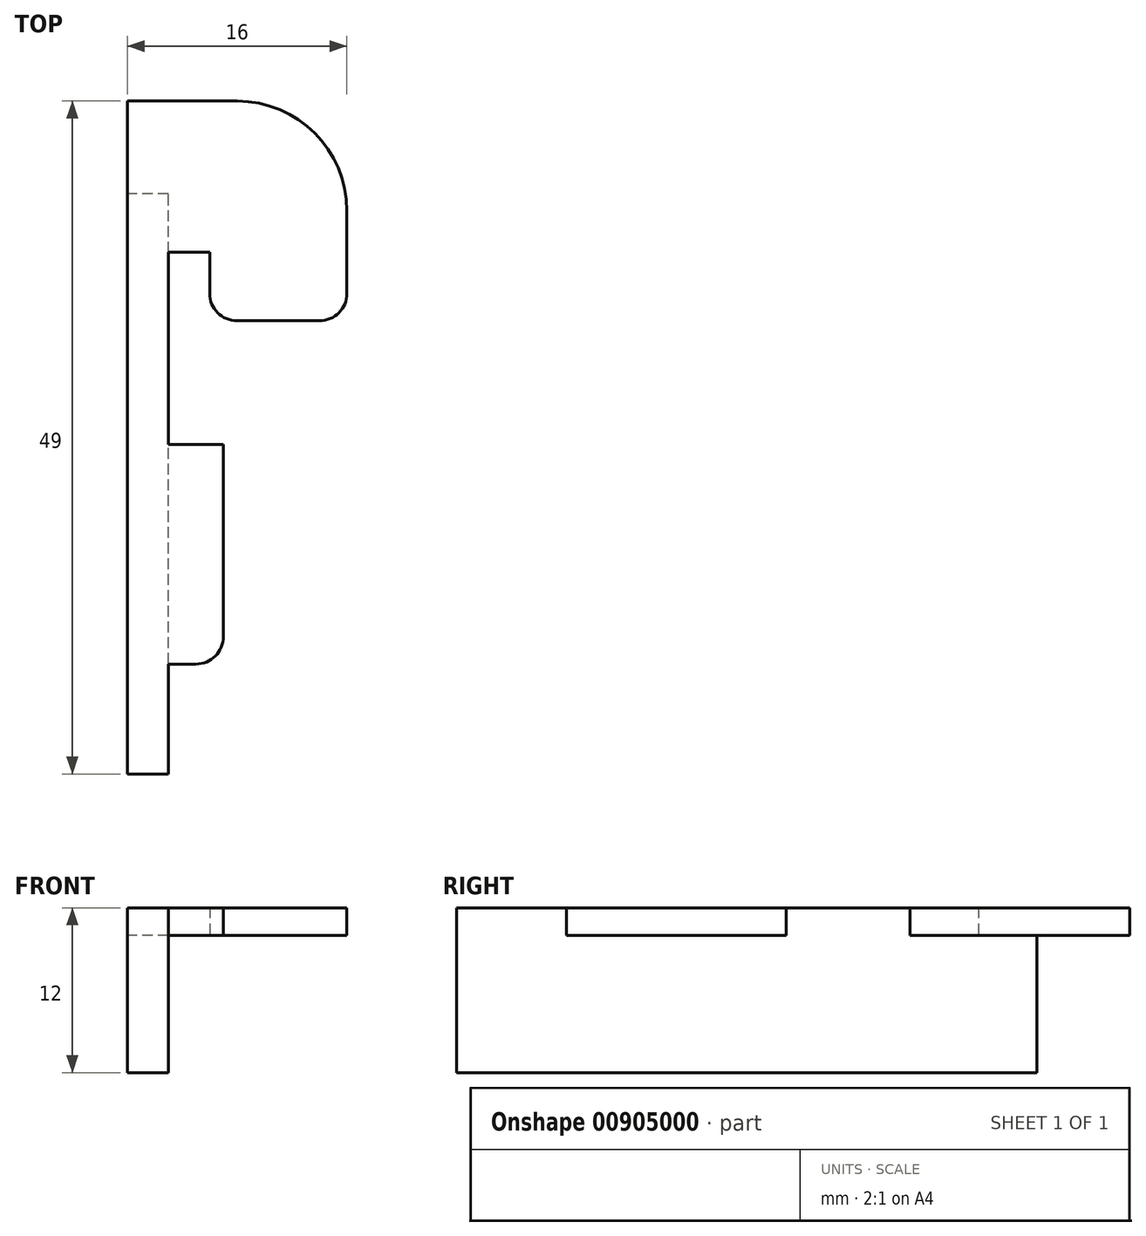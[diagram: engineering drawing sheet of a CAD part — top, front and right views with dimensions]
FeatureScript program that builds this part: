
annotation { "Feature Type Name" : "Feature", "Feature Type Description" : "" }
export const myFeature = defineFeature(function(context is Context, id is Id, definition is map)
    precondition{}
    {
        {
            var Q0;
            Q0=qCreatedBy(makeId("Top.planeOp"),FACE);
            var sketch = newSketch(context, id + "F0", { "sketchPlane" : qUnion([Q0])});
            skLineSegment(sketch, "E0", {"start": v(5, 25) * mm, "end": v(5, -24) * mm});
            skLineSegment(sketch, "E1", {"start": v(5, -24) * mm, "end": v(8, -24) * mm});
            skLineSegment(sketch, "E2", {"start": v(8, -24) * mm, "end": v(8, -16) * mm});
            skLineSegment(sketch, "E3", {"start": v(8, -16) * mm, "end": v(12, -16) * mm});
            skLineSegment(sketch, "E4", {"start": v(12, -16) * mm, "end": v(12, 0) * mm});
            skLineSegment(sketch, "E5", {"start": v(12, 0) * mm, "end": v(8, 0) * mm});
            skLineSegment(sketch, "E6", {"start": v(8, 0) * mm, "end": v(8, 14) * mm});
            skLineSegment(sketch, "E7", {"start": v(21, 9) * mm, "end": v(21, 25) * mm});
            skLineSegment(sketch, "E8", {"start": v(21, 25) * mm, "end": v(5, 25) * mm});
            skLineSegment(sketch, "E9", {"start": v(8, 14) * mm, "end": v(11, 14) * mm});
            skLineSegment(sketch, "E10", {"start": v(11, 14) * mm, "end": v(11, 9) * mm});
            skLineSegment(sketch, "E11", {"start": v(11, 9) * mm, "end": v(21, 9) * mm});
            skSolve(sketch);
        }
        {
            var Q0;
            Q0=makeQuery(id+"F0.imprint","IMPRINT",FACE,{"disambiguationData":[TD([[makeQuery(id+"F0.imprint","IMPRINT",EDGE,{"derivedFrom":sQuery(id+"F0.wireOp",EDGE,"E0")}),1.0]])]});
            extrude(context, id + "F1", {"entities" : qUnion([Q0]), "depth" : 2 * mm});
        }
        {
            var Q0;
            Q0=makeQuery(id+"F1.opExtrude","SWEPT_EDGE",EDGE,{"disambiguationData":[OSD([sQuery(id+"F0.wireOp",EDGE,"E7"),sQuery(id+"F0.wireOp",EDGE,"E8")])]});
            fillet(context, id + "F2", {"entities" : qUnion([Q0]), "radius" : 8 * mm, "tangentPropagation" : true, "allowEdgeOverflow" : false});
        }
        {
            var Q0;
            Q0=makeQuery(id+"F1.opExtrude","SWEPT_EDGE",EDGE,{"disambiguationData":[OSD([sQuery(id+"F0.wireOp",EDGE,"E7"),sQuery(id+"F0.wireOp",EDGE,"E11")])]});
            var Q1;
            Q1=makeQuery(id+"F1.opExtrude","SWEPT_EDGE",EDGE,{"disambiguationData":[OSD([sQuery(id+"F0.wireOp",EDGE,"E3"),sQuery(id+"F0.wireOp",EDGE,"E4")])]});
            var Q2;
            Q2=makeQuery(id+"F1.opExtrude","SWEPT_EDGE",EDGE,{"disambiguationData":[OSD([sQuery(id+"F0.wireOp",EDGE,"E10"),sQuery(id+"F0.wireOp",EDGE,"E11")])]});
            fillet(context, id + "F3", {"entities" : qUnion([Q0, Q1, Q2]), "radius" : 2 * mm, "tangentPropagation" : true, "allowEdgeOverflow" : false});
        }
        {
            var Q0;
            Q0=makeQuery(id+"F1.opExtrude","CAP_FACE",FACE,{"disambiguationData":[OSD([sQuery(id+"F0.wireOp",EDGE,"E0"),sQuery(id+"F0.wireOp",EDGE,"E1"),sQuery(id+"F0.wireOp",EDGE,"E2"),sQuery(id+"F0.wireOp",EDGE,"E3"),sQuery(id+"F0.wireOp",EDGE,"E4"),sQuery(id+"F0.wireOp",EDGE,"E5"),sQuery(id+"F0.wireOp",EDGE,"E6"),sQuery(id+"F0.wireOp",EDGE,"E7"),sQuery(id+"F0.wireOp",EDGE,"E8"),sQuery(id+"F0.wireOp",EDGE,"E9"),sQuery(id+"F0.wireOp",EDGE,"E10"),sQuery(id+"F0.wireOp",EDGE,"E11")])],"isStart":true});
            var sketch = newSketch(context, id + "F4", { "sketchPlane" : qUnion([Q0])});
            skLineSegment(sketch, "E12.bottom", {"start": v(8, 24) * mm, "end": v(5, 24) * mm});
            skLineSegment(sketch, "E12.top", {"start": v(8, -18.24) * mm, "end": v(5, -18.24) * mm});
            skLineSegment(sketch, "E12.left", {"start": v(8, 24) * mm, "end": v(8, -18.24) * mm});
            skLineSegment(sketch, "E12.right", {"start": v(5, 24) * mm, "end": v(5, -18.24) * mm});
            skSolve(sketch);
        }
        {
            var Q0;
            Q0=qSketchRegion(id+"F4",true);
            extrude(context, id + "F5", {"entities" : qUnion([Q0]), "operationType" : NewBodyOperationType.ADD, "offsetDistance" : 25 * mm, "depth" : 10 * mm});
        }
    });
